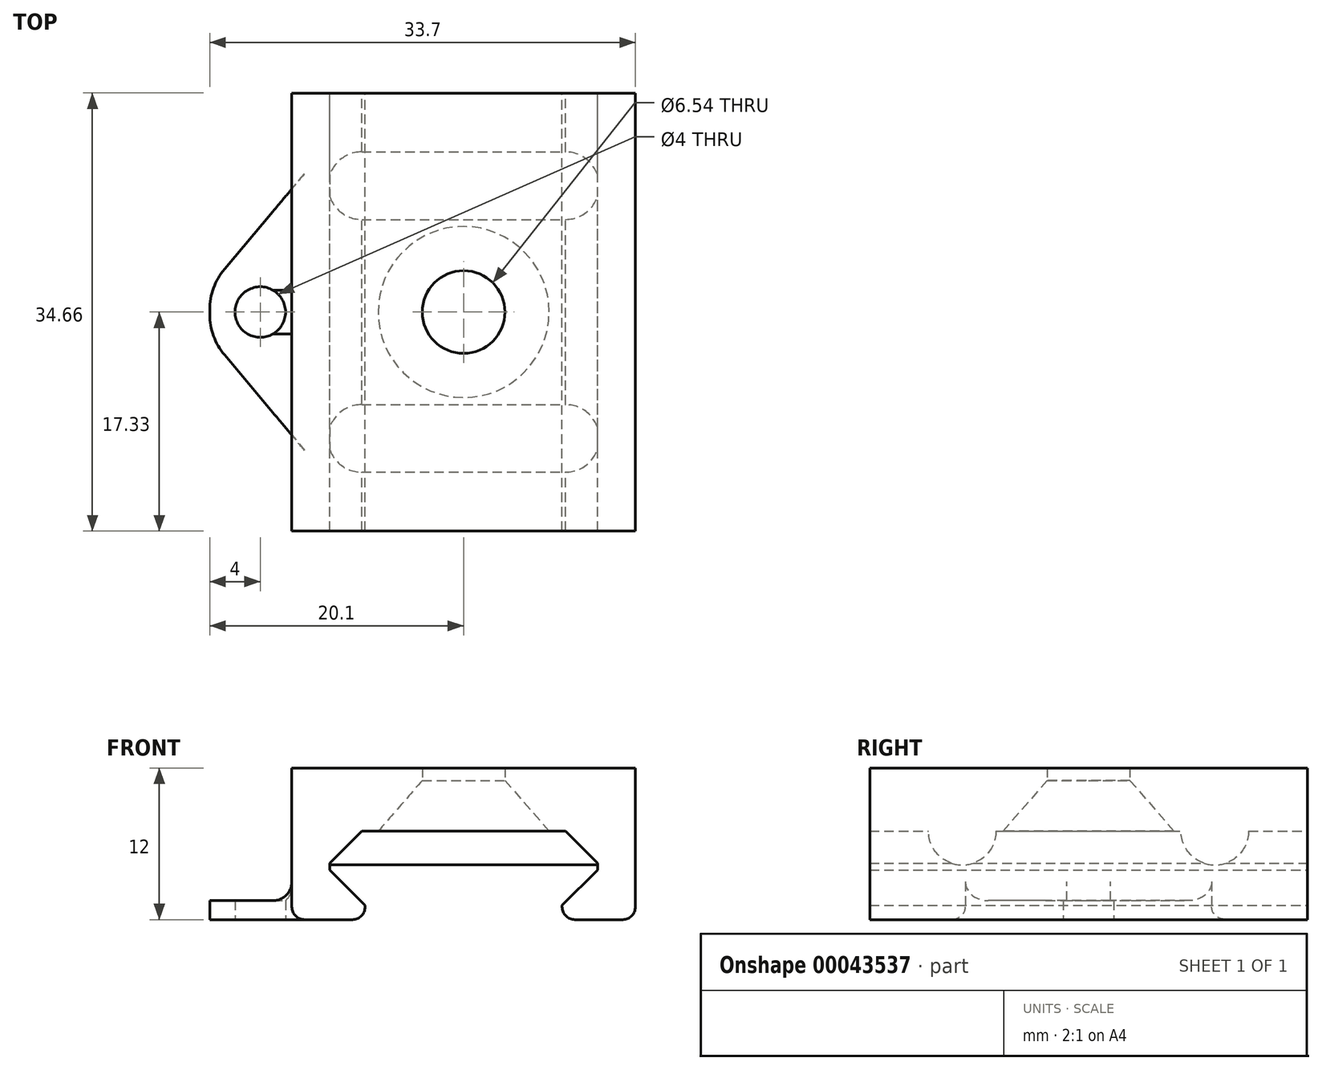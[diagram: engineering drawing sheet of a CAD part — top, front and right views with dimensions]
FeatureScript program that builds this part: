
annotation { "Feature Type Name" : "Feature", "Feature Type Description" : "" }
export const myFeature = defineFeature(function(context is Context, id is Id, definition is map)
    precondition{}
    {
        {
            var Q0;
            Q0=qCreatedBy(makeId("Front.planeOp"),FACE);
            var sketch = newSketch(context, id + "F0", { "sketchPlane" : qUnion([Q0])});
            skLineSegment(sketch, "E0", {"start": v(-10.6, -2.8) * mm, "end": v(10.6, -2.8) * mm, "construction": true});
            skLineSegment(sketch, "E1", {"start": v(-10.6, -3.07) * mm, "end": v(-10.6, -2.53) * mm});
            skLineSegment(sketch, "E2", {"start": v(-10.6, -2.53) * mm, "end": v(-8.07, 0) * mm});
            skLineSegment(sketch, "E3", {"start": v(-8.07, 0) * mm, "end": v(8.07, 0) * mm});
            skLineSegment(sketch, "E4", {"start": v(8.07, 0) * mm, "end": v(10.6, -2.53) * mm});
            skLineSegment(sketch, "E5", {"start": v(10.6, -2.53) * mm, "end": v(10.6, -3.07) * mm});
            skLineSegment(sketch, "E6", {"start": v(10.6, -3.07) * mm, "end": v(7.8, -5.87) * mm});
            skLineSegment(sketch, "E7", {"start": v(7.8, -5.87) * mm, "end": v(7.8, -7) * mm});
            skLineSegment(sketch, "E8", {"start": v(-7.8, -7) * mm, "end": v(-7.8, -5.87) * mm});
            skLineSegment(sketch, "E9", {"start": v(-7.8, -5.87) * mm, "end": v(-10.6, -3.07) * mm});
            skLineSegment(sketch, "E10", {"start": v(0, 0) * mm, "end": v(0, -7) * mm, "construction": true});
            skLineSegment(sketch, "E11", {"start": v(-8.07, 0) * mm, "end": v(-17.76, 0) * mm, "construction": true});
            skLineSegment(sketch, "E12", {"start": v(8.07, 0) * mm, "end": v(18.28, 0) * mm, "construction": true});
            skLineSegment(sketch, "E13", {"start": v(7.8, -7) * mm, "end": v(7.8, 0) * mm, "construction": true});
            skLineSegment(sketch, "E14", {"start": v(-9.5, -4.17) * mm, "end": v(9.5, -4.17) * mm, "construction": true});
            skLineSegment(sketch, "E15", {"start": v(9.5, -1.43) * mm, "end": v(-9.5, -1.43) * mm, "construction": true});
            skLineSegment(sketch, "E16", {"start": v(-9.5, -1.43) * mm, "end": v(-9.5, -4.17) * mm, "construction": true});
            skLineSegment(sketch, "E17", {"start": v(9.5, -1.43) * mm, "end": v(9.5, -4.17) * mm, "construction": true});
            skLineSegment(sketch, "E18", {"start": v(9.5, -4.17) * mm, "end": v(9.5, 0) * mm, "construction": true});
            skPoint(sketch, "E19.visualSharp", {"position": v(-7.8, -7) * mm});
            skPoint(sketch, "E20.visualSharp", {"position": v(7.8, -7) * mm});
            skLineSegment(sketch, "E21", {"start": v(-7.8, -5.87) * mm, "end": v(7.8, -5.87) * mm, "construction": true});
            skLineSegment(sketch, "E22", {"start": v(-7.8, -7) * mm, "end": v(7.8, -7) * mm, "construction": true});
            skPoint(sketch, "E23", {"position": v(0, -7) * mm});
            skLineSegment(sketch, "E24", {"start": v(-7.8, -7) * mm, "end": v(-13.6, -7) * mm});
            skLineSegment(sketch, "E25", {"start": v(-13.6, -7) * mm, "end": v(-13.6, 5) * mm});
            skLineSegment(sketch, "E26", {"start": v(-13.6, 5) * mm, "end": v(13.6, 5) * mm});
            skLineSegment(sketch, "E27", {"start": v(13.6, 5) * mm, "end": v(13.6, -7) * mm});
            skLineSegment(sketch, "E28", {"start": v(13.6, -7) * mm, "end": v(7.8, -7) * mm});
            skLineSegment(sketch, "E29", {"start": v(10.6, -2.8) * mm, "end": v(13.6, -2.8) * mm, "construction": true});
            skLineSegment(sketch, "E30", {"start": v(-10.6, -2.8) * mm, "end": v(-13.6, -2.8) * mm, "construction": true});
            skLineSegment(sketch, "E31", {"start": v(-8.07, 0) * mm, "end": v(-8.07, 5) * mm, "construction": true});
            skSolve(sketch);
        }
        {
            var Q0;
            Q0=qSketchRegion(id+"F0",true);
            extrude(context, id + "F1", {"entities" : qUnion([Q0]), "depth" : (40 - 5.35) * mm});
        }
        {
            var Q0;
            Q0=makeQuery(id+"F1.opExtrude","SWEPT_BODY",BODY,{"disambiguationData":[OSD([sQuery(id+"F0.wireOp",EDGE,"E1"),sQuery(id+"F0.wireOp",EDGE,"E2"),sQuery(id+"F0.wireOp",EDGE,"E3"),sQuery(id+"F0.wireOp",EDGE,"E4"),sQuery(id+"F0.wireOp",EDGE,"E5"),sQuery(id+"F0.wireOp",EDGE,"E6"),sQuery(id+"F0.wireOp",EDGE,"E7"),sQuery(id+"F0.wireOp",EDGE,"E8"),sQuery(id+"F0.wireOp",EDGE,"E9"),sQuery(id+"F0.wireOp",EDGE,"E24"),sQuery(id+"F0.wireOp",EDGE,"E25"),sQuery(id+"F0.wireOp",EDGE,"E26"),sQuery(id+"F0.wireOp",EDGE,"E27"),sQuery(id+"F0.wireOp",EDGE,"E28")])]});
            transform(context, id + "F2", {"entities" : qUnion([Q0]), "transformType" : TransformType.TRANSLATION_3D, "dx" : 0 * mm, "dy" : ((40 - 5.35) / 2) * mm, "dz" : 0 * mm, "makeCopy" : false});
        }
        {
            var Q0;
            Q0=makeQuery(id+"F1.opExtrude","SWEPT_EDGE",EDGE,{"disambiguationData":[OSD([sQuery(id+"F0.wireOp",EDGE,"E8"),sQuery(id+"F0.wireOp",EDGE,"E24")])]});
            var Q1;
            Q1=makeQuery(id+"F1.opExtrude","SWEPT_EDGE",EDGE,{"disambiguationData":[OSD([sQuery(id+"F0.wireOp",EDGE,"E7"),sQuery(id+"F0.wireOp",EDGE,"E28")])]});
            fillet(context, id + "F3", {"entities" : qUnion([Q0, Q1]), "radius" : 1 * mm, "allowEdgeOverflow" : false});
        }
        {
            var Q0;
            Q0=makeQuery(id+"F1.opExtrude","SWEPT_FACE",FACE,{"disambiguationData":[OSD([sQuery(id+"F0.wireOp",EDGE,"E3")])]});
            var sketch = newSketch(context, id + "F4", { "sketchPlane" : qUnion([Q0])});
            skPoint(sketch, "E32", {"position": v(0, 0) * mm});
            skSolve(sketch);
        }
        {
            var Q0;
            Q0=qCreatedBy(makeId("Right.planeOp"),FACE);
            var sketch = newSketch(context, id + "F5", { "sketchPlane" : qUnion([Q0])});
            skLineSegment(sketch, "E33", {"start": v(0, -2.88) * mm, "end": v(0, 8.77) * mm});
            skLineSegment(sketch, "E34", {"start": v(0, 8.77) * mm, "end": v(3.17, 8.77) * mm});
            skLineSegment(sketch, "E35", {"start": v(3.17, 8.77) * mm, "end": v(3.18, 4.13) * mm, "construction": true});
            skLineSegment(sketch, "E36", {"start": v(3.18, 4.13) * mm, "end": v(6.77, 4.13) * mm, "construction": true});
            skLineSegment(sketch, "E37", {"start": v(6.77, -2.88) * mm, "end": v(0, -2.88) * mm});
            skLineSegment(sketch, "E38", {"start": v(3.18, 4.13) * mm, "end": v(6.77, 0) * mm});
            skLineSegment(sketch, "E39", {"start": v(6.77, 0) * mm, "end": v(0, 0) * mm});
            skLineSegment(sketch, "E40", {"start": v(6.77, -2.88) * mm, "end": v(6.77, 0) * mm});
            skLineSegment(sketch, "E41", {"start": v(6.77, 4.13) * mm, "end": v(6.77, 0) * mm, "construction": true});
            skLineSegment(sketch, "E42", {"start": v(3.27, 8.77) * mm, "end": v(3.27, 4.02) * mm});
            skLineSegment(sketch, "E43", {"start": v(0, 8.77) * mm, "end": v(3.27, 8.77) * mm});
            skSolve(sketch);
        }
        {
            var Q0;
            Q0=qSketchRegion(id+"F5",true);
            var Q1;
            Q1=sQuery(id+"F5.wireOp",EDGE,"E33");
            revolve(context, id + "F6", {"entities" : qUnion([Q0]), "axis" : qUnion([Q1]), "revolveType" : RevolveType.FULL});
        }
        {
            var Q0;
            Q0=makeQuery(id+"F6.opRevolve","SWEPT_BODY",BODY,{"disambiguationData":[OSD([sQuery(id+"F5.wireOp",EDGE,"E33"),sQuery(id+"F5.wireOp",EDGE,"E37"),sQuery(id+"F5.wireOp",EDGE,"E38"),sQuery(id+"F5.wireOp",EDGE,"E40"),sQuery(id+"F5.wireOp",EDGE,"E42"),sQuery(id+"F5.wireOp",EDGE,"E43")])]});
            var Q1;
            Q1=makeQuery(id+"F1.opExtrude","SWEPT_BODY",BODY,{"disambiguationData":[OSD([sQuery(id+"F0.wireOp",EDGE,"E1"),sQuery(id+"F0.wireOp",EDGE,"E2"),sQuery(id+"F0.wireOp",EDGE,"E3"),sQuery(id+"F0.wireOp",EDGE,"E4"),sQuery(id+"F0.wireOp",EDGE,"E5"),sQuery(id+"F0.wireOp",EDGE,"E6"),sQuery(id+"F0.wireOp",EDGE,"E7"),sQuery(id+"F0.wireOp",EDGE,"E8"),sQuery(id+"F0.wireOp",EDGE,"E9"),sQuery(id+"F0.wireOp",EDGE,"E24"),sQuery(id+"F0.wireOp",EDGE,"E25"),sQuery(id+"F0.wireOp",EDGE,"E26"),sQuery(id+"F0.wireOp",EDGE,"E27"),sQuery(id+"F0.wireOp",EDGE,"E28")])]});
            booleanBodies(context, id + "F7", {"operationType" : BooleanOperationType.SUBTRACTION, "tools" : qUnion([Q0]), "targets" : qUnion([Q1])});
        }
        {
            var Q0;
            Q0=makeQuery(id+"F1.opExtrude","SWEPT_EDGE",EDGE,{"disambiguationData":[OSD([sQuery(id+"F0.wireOp",EDGE,"E24"),sQuery(id+"F0.wireOp",EDGE,"E25")])]});
            var Q1;
            Q1=makeQuery(id+"F1.opExtrude","SWEPT_EDGE",EDGE,{"disambiguationData":[OSD([sQuery(id+"F0.wireOp",EDGE,"E27"),sQuery(id+"F0.wireOp",EDGE,"E28")])]});
            fillet(context, id + "F8", {"entities" : qUnion([Q0, Q1]), "radius" : 1 * mm, "allowEdgeOverflow" : false});
        }
        {
            var Q0;
            Q0=makeQuery(id+"F1.opExtrude","SWEPT_FACE",FACE,{"disambiguationData":[OSD([sQuery(id+"F0.wireOp",EDGE,"E27")])]});
            var sketch = newSketch(context, id + "F9", { "sketchPlane" : qUnion([Q0])});
            skLineSegment(sketch, "E44.0", {"start": v(-17.32, 0) * mm, "end": v(17.32, 0) * mm, "construction": true});
            skLineSegment(sketch, "E45", {"start": v(-17.32, 0) * mm, "end": v(-12.67, 0) * mm, "construction": true});
            skLineSegment(sketch, "E46", {"start": v(-12.67, 0) * mm, "end": v(-7.32, 0) * mm});
            skLineSegment(sketch, "E47.MirrorCS", {"start": v(12.67, 0) * mm, "end": v(7.32, 0) * mm});
            skLineSegment(sketch, "E48.MirrorCS", {"start": v(17.32, 0) * mm, "end": v(12.67, 0) * mm, "construction": true});
            skLineSegment(sketch, "E49", {"start": v(-7.32, 0) * mm, "end": v(-2.67, 0) * mm, "construction": true});
            skLineSegment(sketch, "E50", {"start": v(-2.67, 0) * mm, "end": v(2.68, 0) * mm});
            skLineSegment(sketch, "E51", {"start": v(2.68, 0) * mm, "end": v(7.32, 0) * mm, "construction": true});
            skArc(sketch, "E52", {"start": v(-12.67, 0) * mm, "mid": v(-11.9, -1.9) * mm, "end": v(-10, -2.67) * mm});
            skArc(sketch, "E53", {"start": v(-7.32, 0) * mm, "mid": v(-8.1, -1.9) * mm, "end": v(-10, -2.67) * mm});
            skLineSegment(sketch, "E54", {"start": v(-10, 0) * mm, "end": v(-10, -2.67) * mm, "construction": true});
            skArc(sketch, "E55.MirrorCS", {"start": v(12.67, 0) * mm, "mid": v(11.9, -1.9) * mm, "end": v(10, -2.67) * mm});
            skLineSegment(sketch, "E56.MirrorCS", {"start": v(10, 0) * mm, "end": v(10, -2.67) * mm, "construction": true});
            skArc(sketch, "E57.MirrorCS", {"start": v(7.32, 0) * mm, "mid": v(8.1, -1.9) * mm, "end": v(10, -2.67) * mm});
            skSolve(sketch);
        }
        {
            var Q0;
            Q0=qSketchRegion(id+"F9",true);
            var Q1;
            Q1=makeQuery(id+"F1.opExtrude","SWEPT_FACE",FACE,{"disambiguationData":[OSD([sQuery(id+"F0.wireOp",EDGE,"E25")])]});
            extrude(context, id + "F10", {"entities" : qUnion([Q0]), "operationType" : NewBodyOperationType.ADD, "endBound" : BoundingType.UP_TO_SURFACE, "oppositeDirection" : true, "endBoundEntityFace" : qUnion([Q1]), "depth" : 25 * mm});
        }
        {
            var Q0;
            Q0=makeQuery(id+"F1.opExtrude","SWEPT_FACE",FACE,{"disambiguationData":[OSD([sQuery(id+"F0.wireOp",EDGE,"E24")])]});
            var sketch = newSketch(context, id + "F11", { "sketchPlane" : qUnion([Q0])});
            skLineSegment(sketch, "E58.0", {"start": v(-12.6, 17.32) * mm, "end": v(-12.6, -17.32) * mm});
            skLineSegment(sketch, "E59", {"start": v(-12.6, 0) * mm, "end": v(-20.1, 0) * mm, "construction": true});
            skPoint(sketch, "E59.endSnap0", {"position": v(-12.6, 0) * mm});
            skLineSegment(sketch, "E60", {"start": v(-20.1, 0.18) * mm, "end": v(-20.1, -0.18) * mm});
            skLineSegment(sketch, "E61", {"start": v(-18.93, -3.4) * mm, "end": v(-12.6, -10.94) * mm});
            skLineSegment(sketch, "E62", {"start": v(-18.93, 3.4) * mm, "end": v(-12.6, 10.94) * mm});
            skLineSegment(sketch, "E63", {"start": v(-20.1, 0) * mm, "end": v(-16.1, 0) * mm, "construction": true});
            skCircle(sketch, "E64", {"center": v(-16.1, 0) * mm, "radius": 2 * mm});
            skPoint(sketch, "E65.visualSharp", {"position": v(-20.1, -2) * mm});
            skArc(sketch, "E65.filletArc", {"start": v(-20.1, -0.18) * mm, "mid": v(-19.8, -1.9) * mm, "end": v(-18.93, -3.4) * mm});
            skPoint(sketch, "E66.visualSharp", {"position": v(-20.1, 2) * mm});
            skArc(sketch, "E66.filletArc", {"start": v(-18.93, 3.4) * mm, "mid": v(-19.8, 1.9) * mm, "end": v(-20.1, 0.18) * mm});
            skSolve(sketch);
        }
        {
            var Q0;
            Q0=qSketchRegion(id+"F11",true);
            extrude(context, id + "F12", {"entities" : qUnion([Q0]), "oppositeDirection" : true, "depth" : 1.5 * mm});
        }
        {
            var Q0;
            Q0=makeQuery(id+"F1.opExtrude","SWEPT_BODY",BODY,{"disambiguationData":[OSD([sQuery(id+"F0.wireOp",EDGE,"E1"),sQuery(id+"F0.wireOp",EDGE,"E2"),sQuery(id+"F0.wireOp",EDGE,"E3"),sQuery(id+"F0.wireOp",EDGE,"E4"),sQuery(id+"F0.wireOp",EDGE,"E5"),sQuery(id+"F0.wireOp",EDGE,"E6"),sQuery(id+"F0.wireOp",EDGE,"E7"),sQuery(id+"F0.wireOp",EDGE,"E8"),sQuery(id+"F0.wireOp",EDGE,"E9"),sQuery(id+"F0.wireOp",EDGE,"E24"),sQuery(id+"F0.wireOp",EDGE,"E25"),sQuery(id+"F0.wireOp",EDGE,"E26"),sQuery(id+"F0.wireOp",EDGE,"E27"),sQuery(id+"F0.wireOp",EDGE,"E28")])]});
            var Q1;
            Q1=makeQuery(id+"F12.opExtrude","SWEPT_BODY",BODY,{"disambiguationData":[OSD([sQuery(id+"F11.wireOp",EDGE,"E58.0"),sQuery(id+"F11.wireOp",EDGE,"E60"),sQuery(id+"F11.wireOp",EDGE,"E61"),sQuery(id+"F11.wireOp",EDGE,"E62")])]});
            booleanBodies(context, id + "F13", {"operationType" : BooleanOperationType.UNION, "tools" : qUnion([Q0, Q1])});
        }
        {
            var Q0;
            Q0=makeQuery(id+"F13.opBoolean","INTERSECT",EDGE,{"derivedFrom":[makeQuery(id+"F1.opExtrude","SWEPT_FACE",FACE,{"disambiguationData":[OSD([sQuery(id+"F0.wireOp",EDGE,"E25")])]}),makeQuery(id+"F12.opExtrude","CAP_FACE",FACE,{"disambiguationData":[OSD([sQuery(id+"F11.wireOp",EDGE,"E58.0"),sQuery(id+"F11.wireOp",EDGE,"E60"),sQuery(id+"F11.wireOp",EDGE,"E61"),sQuery(id+"F11.wireOp",EDGE,"E62")])],"isStart":false})]});
            fillet(context, id + "F14", {"entities" : qUnion([Q0]), "radius" : 1.5 * mm, "allowEdgeOverflow" : false});
        }
    });
